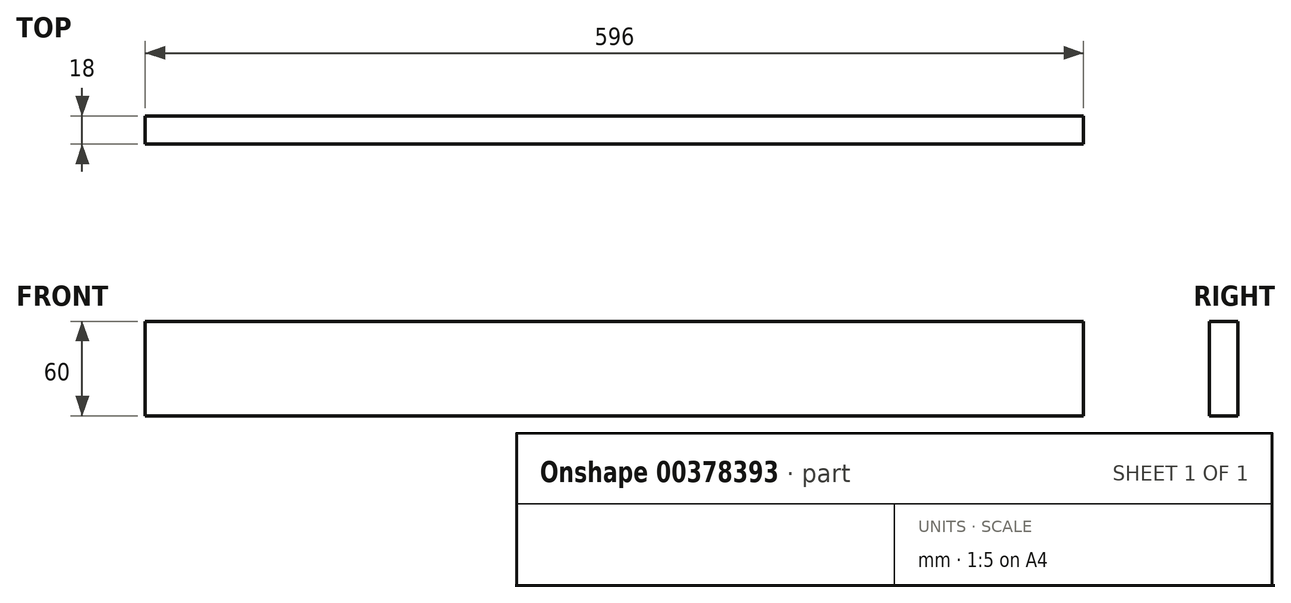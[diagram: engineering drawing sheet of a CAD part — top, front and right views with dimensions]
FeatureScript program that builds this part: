
annotation { "Feature Type Name" : "Feature", "Feature Type Description" : "" }
export const myFeature = defineFeature(function(context is Context, id is Id, definition is map)
    precondition{}
    {
        {
            var Q0;
            Q0=qCreatedBy(makeId("Right.planeOp"),FACE);
            var sketch = newSketch(context, id + "F0", { "sketchPlane" : qUnion([Q0])});
            skLineSegment(sketch, "E0.bottom", {"start": v(9, 30) * mm, "end": v(-9, 30) * mm});
            skLineSegment(sketch, "E0.top", {"start": v(9, -30) * mm, "end": v(-9, -30) * mm});
            skLineSegment(sketch, "E0.left", {"start": v(9, 30) * mm, "end": v(9, -30) * mm});
            skLineSegment(sketch, "E0.right", {"start": v(-9, 30) * mm, "end": v(-9, -30) * mm});
            skPoint(sketch, "E0.middle", {"position": v(0, 0) * mm});
            skSolve(sketch);
        }
        {
            var Q0;
            Q0 = qSketchRegion(id + "F0", true);
            extrude(context, id + "F1", {"entities" : qUnion([Q0]), "depth" : 596 * mm});
        }
    });
